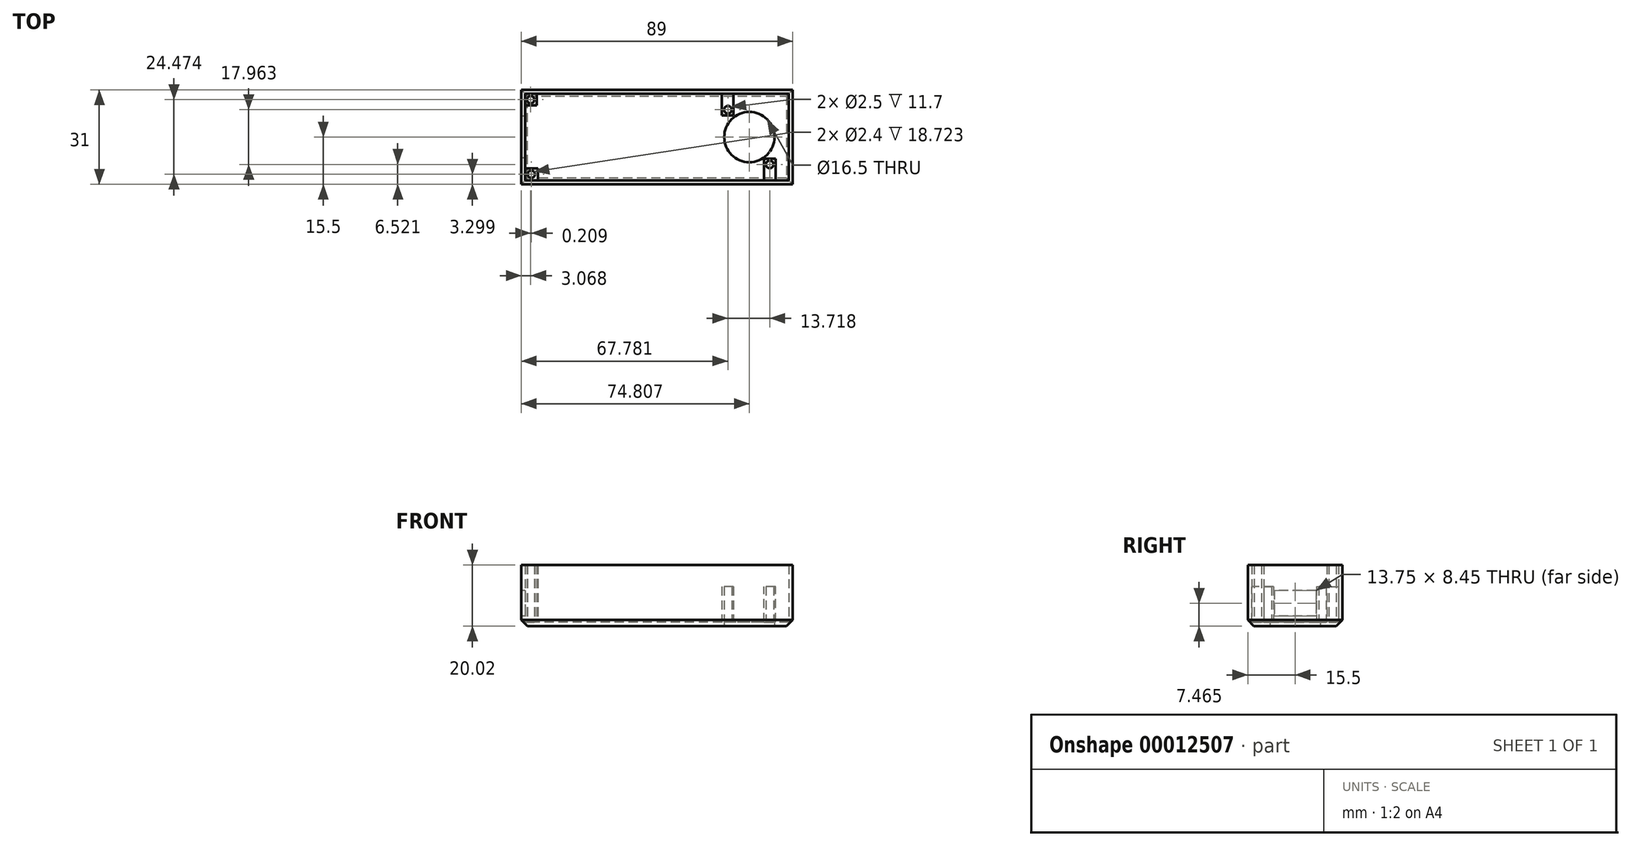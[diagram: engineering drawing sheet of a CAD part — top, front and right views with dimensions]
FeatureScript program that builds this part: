
annotation { "Feature Type Name" : "Feature", "Feature Type Description" : "" }
export const myFeature = defineFeature(function(context is Context, id is Id, definition is map)
    precondition{}
    {
        {
            var Q0;
            Q0=qCreatedBy(makeId("Top.planeOp"),FACE);
            var sketch = newSketch(context, id + "F0", { "sketchPlane" : qUnion([Q0])});
            skLineSegment(sketch, "E0.rect.bottom", {"start": v(44.5, 15.5) * mm, "end": v(-44.5, 15.5) * mm});
            skLineSegment(sketch, "E0.rect.top", {"start": v(44.5, -15.5) * mm, "end": v(-44.5, -15.5) * mm});
            skLineSegment(sketch, "E0.rect.left", {"start": v(44.5, 15.5) * mm, "end": v(44.5, -15.5) * mm});
            skLineSegment(sketch, "E0.rect.right", {"start": v(-44.5, 15.5) * mm, "end": v(-44.5, -15.5) * mm});
            skPoint(sketch, "E0.rect.middle", {"position": v(0, 0) * mm});
            skSolve(sketch);
        }
        {
            var Q0;
            Q0=makeQuery(id+"F0.imprint","IMPRINT",FACE,{"disambiguationData":[TD([[makeQuery(id+"F0.imprint","IMPRINT",EDGE,{"derivedFrom":sQuery(id+"F0.wireOp",EDGE,"E0.rect.bottom")}),1.0]])]});
            extrude(context, id + "F1", {"entities" : qUnion([Q0]), "depth" : 20 * mm});
        }
        {
            var Q0;
            Q0=qCreatedBy(makeId("Top.planeOp"),FACE);
            var sketch = newSketch(context, id + "F2", { "sketchPlane" : qUnion([Q0])});
            skCircle(sketch, "E1", {"center": v(30.3, 0) * mm, "radius": 8.25 * mm});
            skSolve(sketch);
        }
        {
            var Q0;
            Q0=makeQuery(id+"F1.opExtrude","CAP_FACE",FACE,{"disambiguationData":[OSD([sQuery(id+"F0.wireOp",EDGE,"E0.rect.bottom"),sQuery(id+"F0.wireOp",EDGE,"E0.rect.top"),sQuery(id+"F0.wireOp",EDGE,"E0.rect.left"),sQuery(id+"F0.wireOp",EDGE,"E0.rect.right")])],"isStart":false});
            shell(context, id + "F3", {"entities" : qUnion([Q0]), "thickness" : 1.3 * mm});
        }
        {
            var Q0;
            Q0=makeQuery(id+"F2.imprint","IMPRINT",FACE,{"disambiguationData":[TD([[makeQuery(id+"F2.imprint","IMPRINT",EDGE,{"derivedFrom":sQuery(id+"F2.wireOp",EDGE,"E1")}),1.0]])]});
            extrude(context, id + "F4", {"entities" : qUnion([Q0]), "operationType" : NewBodyOperationType.REMOVE, "depth" : 33.4 * mm});
        }
        {
            var Q0;
            Q0=qCreatedBy(makeId("Top.planeOp"),FACE);
            var sketch = newSketch(context, id + "F5", { "sketchPlane" : qUnion([Q0])});
            skLineSegment(sketch, "E2.bottom", {"start": v(19.06, 14.33) * mm, "end": v(38.93, 14.33) * mm});
            skLineSegment(sketch, "E2.top", {"start": v(19.06, -15.34) * mm, "end": v(38.93, -15.34) * mm});
            skLineSegment(sketch, "E2.left", {"start": v(19.06, 14.33) * mm, "end": v(19.06, -15.34) * mm});
            skLineSegment(sketch, "E2.right", {"start": v(38.93, 14.33) * mm, "end": v(38.93, -15.34) * mm});
            skLineSegment(sketch, "E3.bottom", {"start": v(38.93, -7.13) * mm, "end": v(35.15, -7.13) * mm});
            skLineSegment(sketch, "E3.top", {"start": v(38.93, -15.34) * mm, "end": v(35.15, -15.34) * mm});
            skLineSegment(sketch, "E3.left", {"start": v(38.93, -7.13) * mm, "end": v(38.93, -15.34) * mm});
            skLineSegment(sketch, "E3.right", {"start": v(35.15, -7.13) * mm, "end": v(35.15, -15.34) * mm});
            skLineSegment(sketch, "E4.bottom", {"start": v(19.06, 7.06) * mm, "end": v(21.33, 7.06) * mm});
            skLineSegment(sketch, "E4.top", {"start": v(19.06, 14.33) * mm, "end": v(21.33, 14.33) * mm});
            skLineSegment(sketch, "E4.left", {"start": v(19.06, 7.06) * mm, "end": v(19.06, 14.33) * mm});
            skLineSegment(sketch, "E4.right", {"start": v(21.33, 7.06) * mm, "end": v(21.33, 14.33) * mm});
            skLineSegment(sketch, "E5.bottom", {"start": v(21.33, 7.06) * mm, "end": v(25.11, 7.06) * mm});
            skLineSegment(sketch, "E5.top", {"start": v(21.33, 14.33) * mm, "end": v(25.11, 14.33) * mm});
            skLineSegment(sketch, "E5.right", {"start": v(25.11, 7.06) * mm, "end": v(25.11, 14.33) * mm});
            skCircle(sketch, "E6", {"center": v(23.28, 8.98) * mm, "radius": 1.25 * mm});
            skCircle(sketch, "E7", {"center": v(37, -8.98) * mm, "radius": 1.25 * mm});
            skSolve(sketch);
        }
        {
            var Q0;
            Q0=makeQuery(id+"F5.imprint","IMPRINT",FACE,{"disambiguationData":[TD([[makeQuery(id+"F5.imprint","IMPRINT",EDGE,{"derivedFrom":sQuery(id+"F5.wireOp",EDGE,"E5.bottom")}),1.0]])]});
            var Q1;
            Q1=makeQuery(id+"F5.imprint","IMPRINT",FACE,{"disambiguationData":[TD([[makeQuery(id+"F5.imprint","IMPRINT",EDGE,{"derivedFrom":sQuery(id+"F5.wireOp",EDGE,"E3.bottom")}),1.0]])]});
            extrude(context, id + "F6", {"entities" : qUnion([Q0, Q1]), "operationType" : NewBodyOperationType.ADD, "depth" : 13 * mm});
        }
        {
            var Q0;
            Q0=makeQuery(id+"F1.opExtrude","CAP_EDGE",EDGE,{"disambiguationData":[OSD([sQuery(id+"F0.wireOp",EDGE,"E0.rect.top")])],"isStart":true});
            var Q1;
            Q1=makeQuery(id+"F1.opExtrude","CAP_EDGE",EDGE,{"disambiguationData":[OSD([sQuery(id+"F0.wireOp",EDGE,"E0.rect.left")])],"isStart":true});
            var Q2;
            Q2=makeQuery(id+"F1.opExtrude","CAP_EDGE",EDGE,{"disambiguationData":[OSD([sQuery(id+"F0.wireOp",EDGE,"E0.rect.bottom")])],"isStart":true});
            var Q3;
            Q3=makeQuery(id+"F1.opExtrude","CAP_EDGE",EDGE,{"disambiguationData":[OSD([sQuery(id+"F0.wireOp",EDGE,"E0.rect.right")])],"isStart":true});
            chamfer(context, id + "F7", {"entities" : qUnion([Q0, Q1, Q2, Q3]), "width" : 2 * mm, "tangentPropagation" : true});
        }
        {
            var Q0;
            Q0=makeQuery(id+"F1.opExtrude","SWEPT_FACE",FACE,{"disambiguationData":[OSD([sQuery(id+"F0.wireOp",EDGE,"E0.rect.right")])]});
            var sketch = newSketch(context, id + "F8", { "sketchPlane" : qUnion([Q0])});
            skLineSegment(sketch, "E8.rect.bottom", {"start": v(6.88, 3.24) * mm, "end": v(-6.88, 3.24) * mm});
            skLineSegment(sketch, "E8.rect.top", {"start": v(6.88, 11.69) * mm, "end": v(-6.88, 11.69) * mm});
            skLineSegment(sketch, "E8.rect.left", {"start": v(6.88, 3.24) * mm, "end": v(6.88, 11.69) * mm});
            skLineSegment(sketch, "E8.rect.right", {"start": v(-6.88, 3.24) * mm, "end": v(-6.88, 11.69) * mm});
            skPoint(sketch, "E8.rect.middle", {"position": v(0, 7.46) * mm});
            skSolve(sketch);
        }
        {
            var Q0;
            Q0=makeQuery(id+"F8.imprint","IMPRINT",FACE,{"disambiguationData":[TD([[makeQuery(id+"F8.imprint","IMPRINT",EDGE,{"derivedFrom":sQuery(id+"F8.wireOp",EDGE,"E8.rect.bottom")}),-1.0]])]});
            extrude(context, id + "F9", {"entities" : qUnion([Q0]), "operationType" : NewBodyOperationType.REMOVE, "oppositeDirection" : true, "depth" : 7.2 * mm});
        }
        {
            var Q0;
            {var subQ0=sQuery(id+"F0.wireOp",EDGE,"E0.rect.bottom");var subQ1=sQuery(id+"F0.wireOp",EDGE,"E0.rect.top");var subQ2=sQuery(id+"F0.wireOp",EDGE,"E0.rect.left");var subQ3=sQuery(id+"F0.wireOp",EDGE,"E0.rect.right");Q0=makeQuery(id+"F6.boolean.opBoolean","SPLIT",FACE,{"disambiguationData":[TD([makeQuery(id+"F4.boolean.opBoolean","COPY",FACE,{"derivedFrom":makeQuery(id+"F4.opExtrude","SWEPT_FACE",FACE,{"disambiguationData":[OSD([sQuery(id+"F2.wireOp",EDGE,"E1")])]})})])],"derivedFrom":makeQuery(id+"F3.opShell","OFFSET_FACE",FACE,{"disambiguationData":[OSD([subQ0,subQ1,subQ2,subQ3])]})});}
            var sketch = newSketch(context, id + "F10", { "sketchPlane" : qUnion([Q0])});
            skSolve(sketch);
        }
        {
            var Q0;
            {var subQ3=sQuery(id+"F0.wireOp",EDGE,"E0.rect.left");Q0=makeQuery(id+"F10.imprint","IMPRINT",FACE,{"disambiguationData":[TD([[makeQuery(id+"F10.imprint","IMPRINT",EDGE,{"derivedFrom":makeQuery(id+"F3.opShell","OFFSET_EDGE",EDGE,{"disambiguationData":[OSD([subQ3]),TDD([makeQuery(id+"F1.opExtrude","CAP_EDGE",EDGE,{"disambiguationData":[OSD([subQ3])],"isStart":true})])]})}),-1.0]])]});}
            var sketch = newSketch(context, id + "F11", { "sketchPlane" : qUnion([Q0])});
            skLineSegment(sketch, "E9.bottom", {"start": v(-39.47, 14.27) * mm, "end": v(-43.25, 14.27) * mm});
            skLineSegment(sketch, "E9.top", {"start": v(-39.47, 10.42) * mm, "end": v(-43.25, 10.42) * mm});
            skLineSegment(sketch, "E9.left", {"start": v(-39.47, 14.27) * mm, "end": v(-39.47, 10.42) * mm});
            skLineSegment(sketch, "E9.right", {"start": v(-43.25, 14.27) * mm, "end": v(-43.25, 10.42) * mm});
            skLineSegment(sketch, "E10.bottom", {"start": v(-43.25, -10.26) * mm, "end": v(-39.1, -10.26) * mm});
            skLineSegment(sketch, "E10.top", {"start": v(-43.25, -14.26) * mm, "end": v(-39.1, -14.26) * mm});
            skLineSegment(sketch, "E10.left", {"start": v(-43.25, -10.26) * mm, "end": v(-43.25, -14.26) * mm});
            skLineSegment(sketch, "E10.right", {"start": v(-39.1, -10.26) * mm, "end": v(-39.1, -14.26) * mm});
            skCircle(sketch, "E11", {"center": v(-41.43, 12.27) * mm, "radius": 1.2 * mm});
            skCircle(sketch, "E12", {"center": v(-41.22, -12.2) * mm, "radius": 1.2 * mm});
            skSolve(sketch);
        }
        {
            var Q0;
            Q0=makeQuery(id+"F11.imprint","IMPRINT",FACE,{"disambiguationData":[TD([[makeQuery(id+"F11.imprint","IMPRINT",EDGE,{"derivedFrom":sQuery(id+"F11.wireOp",EDGE,"E12")}),-1.0]])]});
            var Q1;
            Q1=makeQuery(id+"F11.imprint","IMPRINT",FACE,{"disambiguationData":[TD([[makeQuery(id+"F11.imprint","IMPRINT",EDGE,{"derivedFrom":sQuery(id+"F11.wireOp",EDGE,"E11")}),-1.0]])]});
            extrude(context, id + "F12", {"entities" : qUnion([Q0, Q1]), "operationType" : NewBodyOperationType.ADD, "depth" : 18.72 * mm});
        }
    });
